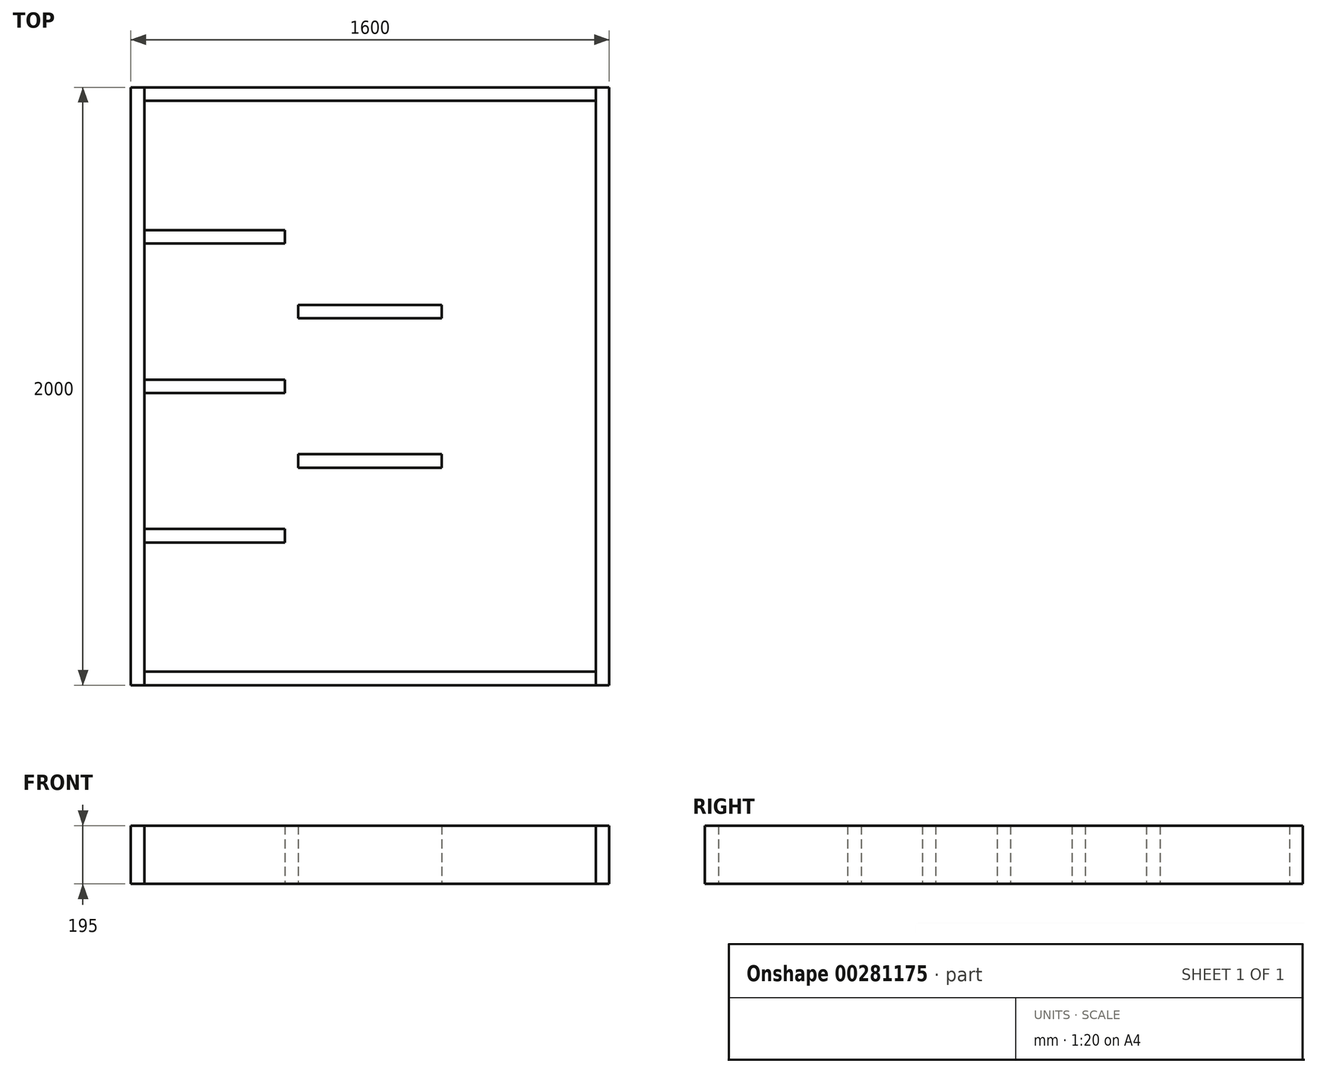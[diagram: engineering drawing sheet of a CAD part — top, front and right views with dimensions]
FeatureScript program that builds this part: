
annotation { "Feature Type Name" : "Feature", "Feature Type Description" : "" }
export const myFeature = defineFeature(function(context is Context, id is Id, definition is map)
    precondition{}
    {
        {
            var Q0;
            Q0=qCreatedBy(makeId("Top.planeOp"),FACE);
            var sketch = newSketch(context, id + "F0", { "sketchPlane" : qUnion([Q0])});
            skLineSegment(sketch, "E0.bottom", {"start": v(0, 0) * mm, "end": v(1700, 0) * mm, "construction": true});
            skLineSegment(sketch, "E0.top", {"start": v(0, 2500) * mm, "end": v(1700, 2500) * mm, "construction": true});
            skLineSegment(sketch, "E0.left", {"start": v(0, 0) * mm, "end": v(0, 2500) * mm, "construction": true});
            skLineSegment(sketch, "E0.right", {"start": v(1700, 0) * mm, "end": v(1700, 2500) * mm, "construction": true});
            skLineSegment(sketch, "E1.bottom", {"start": v(1700, 0) * mm, "end": v(1600, 0) * mm, "construction": true});
            skLineSegment(sketch, "E1.top", {"start": v(1700, 1050) * mm, "end": v(1600, 1050) * mm, "construction": true});
            skLineSegment(sketch, "E1.left", {"start": v(1700, 0) * mm, "end": v(1700, 1050) * mm, "construction": true});
            skLineSegment(sketch, "E1.right", {"start": v(1600, 0) * mm, "end": v(1600, 1050) * mm, "construction": true});
            skSolve(sketch);
        }
        {
            var Q0;
            Q0=qCreatedBy(makeId("Top.planeOp"),FACE);
            cPlane(context, id + "F1", {"entities" : qUnion([Q0]), "cplaneType" : CPlaneType.OFFSET, "offset" : 95 * mm, "width" : 150 * mm, "height" : 150 * mm});
        }
        {
            var Q0;
            Q0=qCreatedBy(id+"F1.planeOp",FACE);
            var sketch = newSketch(context, id + "F2", { "sketchPlane" : qUnion([Q0])});
            skLineSegment(sketch, "E2.bottom", {"start": v(0, 2305) * mm, "end": v(45, 2305) * mm});
            skLineSegment(sketch, "E2.top", {"start": v(0, 305) * mm, "end": v(45, 305) * mm});
            skLineSegment(sketch, "E2.left", {"start": v(0, 2305) * mm, "end": v(0, 305) * mm});
            skLineSegment(sketch, "E2.right", {"start": v(45, 2305) * mm, "end": v(45, 305) * mm});
            skLineSegment(sketch, "E3.bottom", {"start": v(1555, 2305) * mm, "end": v(1600, 2305) * mm});
            skLineSegment(sketch, "E3.top", {"start": v(1555, 305) * mm, "end": v(1600, 305) * mm});
            skLineSegment(sketch, "E3.left", {"start": v(1555, 2305) * mm, "end": v(1555, 305) * mm});
            skLineSegment(sketch, "E3.right", {"start": v(1600, 2305) * mm, "end": v(1600, 305) * mm});
            skLineSegment(sketch, "E4.bottom", {"start": v(45, 305) * mm, "end": v(1555, 305) * mm});
            skLineSegment(sketch, "E4.top", {"start": v(45, 350) * mm, "end": v(1555, 350) * mm});
            skLineSegment(sketch, "E4.left", {"start": v(45, 305) * mm, "end": v(45, 350) * mm});
            skLineSegment(sketch, "E4.right", {"start": v(1555, 305) * mm, "end": v(1555, 350) * mm});
            skLineSegment(sketch, "E5.bottom", {"start": v(45, 2305) * mm, "end": v(1555, 2305) * mm});
            skLineSegment(sketch, "E5.top", {"start": v(45, 2260) * mm, "end": v(1555, 2260) * mm});
            skLineSegment(sketch, "E5.left", {"start": v(45, 2305) * mm, "end": v(45, 2260) * mm});
            skLineSegment(sketch, "E5.right", {"start": v(1555, 2305) * mm, "end": v(1555, 2260) * mm});
            skLineSegment(sketch, "E6.bottom", {"start": v(515, 2260) * mm, "end": v(560, 2260) * mm});
            skLineSegment(sketch, "E6.top", {"start": v(515, 350) * mm, "end": v(560, 350) * mm});
            skLineSegment(sketch, "E6.left", {"start": v(515, 2260) * mm, "end": v(515, 350) * mm});
            skLineSegment(sketch, "E6.right", {"start": v(560, 2260) * mm, "end": v(560, 350) * mm});
            skLineSegment(sketch, "E7.bottom", {"start": v(1040, 2260) * mm, "end": v(1085, 2260) * mm});
            skLineSegment(sketch, "E7.top", {"start": v(1040, 350) * mm, "end": v(1085, 350) * mm});
            skLineSegment(sketch, "E7.left", {"start": v(1040, 2260) * mm, "end": v(1040, 350) * mm});
            skLineSegment(sketch, "E7.right", {"start": v(1085, 2260) * mm, "end": v(1085, 350) * mm});
            skLineSegment(sketch, "E8.bottom", {"start": v(45, 1827.5) * mm, "end": v(515, 1827.5) * mm});
            skLineSegment(sketch, "E8.top", {"start": v(45, 1782.5) * mm, "end": v(515, 1782.5) * mm});
            skLineSegment(sketch, "E8.left", {"start": v(45, 1827.5) * mm, "end": v(45, 1782.5) * mm});
            skLineSegment(sketch, "E8.right", {"start": v(515, 1827.5) * mm, "end": v(515, 1782.5) * mm});
            skLineSegment(sketch, "E9.bottom", {"start": v(45, 1327.5) * mm, "end": v(515, 1327.5) * mm});
            skLineSegment(sketch, "E9.top", {"start": v(45, 1282.5) * mm, "end": v(515, 1282.5) * mm});
            skLineSegment(sketch, "E9.left", {"start": v(45, 1327.5) * mm, "end": v(45, 1282.5) * mm});
            skLineSegment(sketch, "E9.right", {"start": v(515, 1327.5) * mm, "end": v(515, 1282.5) * mm});
            skLineSegment(sketch, "E10.bottom", {"start": v(45, 827.5) * mm, "end": v(515, 827.5) * mm});
            skLineSegment(sketch, "E10.top", {"start": v(45, 782.5) * mm, "end": v(515, 782.5) * mm});
            skLineSegment(sketch, "E10.left", {"start": v(45, 827.5) * mm, "end": v(45, 782.5) * mm});
            skLineSegment(sketch, "E10.right", {"start": v(515, 827.5) * mm, "end": v(515, 782.5) * mm});
            skPoint(sketch, "E11", {"position": v(45, 1305) * mm});
            skPoint(sketch, "E12", {"position": v(45, 805) * mm});
            skPoint(sketch, "E13", {"position": v(45, 1805) * mm});
            skLineSegment(sketch, "E14.bottom", {"start": v(560, 1577.5) * mm, "end": v(1040, 1577.5) * mm});
            skLineSegment(sketch, "E14.top", {"start": v(560, 1532.5) * mm, "end": v(1040, 1532.5) * mm});
            skLineSegment(sketch, "E14.left", {"start": v(560, 1577.5) * mm, "end": v(560, 1532.5) * mm});
            skLineSegment(sketch, "E14.right", {"start": v(1040, 1577.5) * mm, "end": v(1040, 1532.5) * mm});
            skLineSegment(sketch, "E15.bottom", {"start": v(560, 1077.5) * mm, "end": v(1040, 1077.5) * mm});
            skLineSegment(sketch, "E15.top", {"start": v(560, 1032.5) * mm, "end": v(1040, 1032.5) * mm});
            skLineSegment(sketch, "E15.left", {"start": v(560, 1077.5) * mm, "end": v(560, 1032.5) * mm});
            skLineSegment(sketch, "E15.right", {"start": v(1040, 1077.5) * mm, "end": v(1040, 1032.5) * mm});
            skPoint(sketch, "E16", {"position": v(560, 1555) * mm});
            skPoint(sketch, "E17", {"position": v(560, 1055) * mm});
            skLineSegment(sketch, "E18", {"start": v(800, 2260) * mm, "end": v(800, 350) * mm, "construction": true});
            skLineSegment(sketch, "E19.MirrorCS", {"start": v(1085, 827.5) * mm, "end": v(1085, 782.5) * mm});
            skLineSegment(sketch, "E20.MirrorCS", {"start": v(1555, 1827.5) * mm, "end": v(1555, 1782.5) * mm});
            skLineSegment(sketch, "E21.MirrorCS", {"start": v(1085, 1827.5) * mm, "end": v(1085, 1782.5) * mm});
            skLineSegment(sketch, "E22.MirrorCS", {"start": v(1555, 827.5) * mm, "end": v(1555, 782.5) * mm});
            skLineSegment(sketch, "E23.MirrorCS", {"start": v(1085, 1327.5) * mm, "end": v(1085, 1282.5) * mm});
            skLineSegment(sketch, "E24.MirrorCS", {"start": v(1555, 1327.5) * mm, "end": v(1555, 1282.5) * mm});
            skPoint(sketch, "E25.MirrorP", {"position": v(1555, 1305) * mm});
            skPoint(sketch, "E26.MirrorP", {"position": v(1040, 1555) * mm});
            skLineSegment(sketch, "E27.MirrorCS", {"start": v(1555, 1282.5) * mm, "end": v(1085, 1282.5) * mm});
            skPoint(sketch, "E28.MirrorP", {"position": v(1555, 805) * mm});
            skLineSegment(sketch, "E29.MirrorCS", {"start": v(1555, 1782.5) * mm, "end": v(1085, 1782.5) * mm});
            skLineSegment(sketch, "E30.MirrorCS", {"start": v(1555, 1327.5) * mm, "end": v(1085, 1327.5) * mm});
            skLineSegment(sketch, "E31.MirrorCS", {"start": v(1555, 827.5) * mm, "end": v(1085, 827.5) * mm});
            skLineSegment(sketch, "E32.MirrorCS", {"start": v(1555, 1827.5) * mm, "end": v(1085, 1827.5) * mm});
            skPoint(sketch, "E33.MirrorP", {"position": v(1040, 1055) * mm});
            skLineSegment(sketch, "E34.MirrorCS", {"start": v(1555, 782.5) * mm, "end": v(1085, 782.5) * mm});
            skPoint(sketch, "E35.MirrorP", {"position": v(1555, 1805) * mm});
            skSolve(sketch);
        }
        {
            var Q0;
            Q0=makeQuery(id+"F2.imprint","IMPRINT",FACE,{"disambiguationData":[TD([[makeQuery(id+"F2.imprint","IMPRINT",EDGE,{"derivedFrom":sQuery(id+"F2.wireOp",EDGE,"E2.bottom")}),-1.0]])]});
            var Q1;
            {var subQ6=sQuery(id+"F2.wireOp",EDGE,"E6.bottom");Q1=makeQuery(id+"F2.imprint","IMPRINT",FACE,{"disambiguationData":[TD([[makeQuery(id+"F2.imprint","IMPRINT",EDGE,{"derivedFrom":subQ6}),-1.0]])]});}
            var Q2;
            {var subQ6=sQuery(id+"F2.wireOp",EDGE,"E7.bottom");Q2=makeQuery(id+"F2.imprint","IMPRINT",FACE,{"disambiguationData":[TD([[makeQuery(id+"F2.imprint","IMPRINT",EDGE,{"derivedFrom":subQ6}),-1.0]])]});}
            var Q3;
            Q3=makeQuery(id+"F2.imprint","IMPRINT",FACE,{"disambiguationData":[TD([[makeQuery(id+"F2.imprint","IMPRINT",EDGE,{"derivedFrom":sQuery(id+"F2.wireOp",EDGE,"E3.bottom")}),-1.0]])]});
            extrude(context, id + "F3", {"entities" : qUnion([Q0, Q1, Q2, Q3]), "depth" : 195 * mm});
        }
        {
            var Q0;
            Q0=makeQuery(id+"F2.imprint","IMPRINT",FACE,{"disambiguationData":[TD([[makeQuery(id+"F2.imprint","IMPRINT",EDGE,{"derivedFrom":sQuery(id+"F2.wireOp",EDGE,"E5.bottom")}),-1.0]])]});
            var Q1;
            Q1=makeQuery(id+"F2.imprint","IMPRINT",FACE,{"disambiguationData":[TD([[makeQuery(id+"F2.imprint","IMPRINT",EDGE,{"derivedFrom":sQuery(id+"F2.wireOp",EDGE,"E8.bottom")}),-1.0]])]});
            var Q2;
            Q2=makeQuery(id+"F2.imprint","IMPRINT",FACE,{"disambiguationData":[TD([[makeQuery(id+"F2.imprint","IMPRINT",EDGE,{"derivedFrom":sQuery(id+"F2.wireOp",EDGE,"E9.bottom")}),-1.0]])]});
            var Q3;
            Q3=makeQuery(id+"F2.imprint","IMPRINT",FACE,{"disambiguationData":[TD([[makeQuery(id+"F2.imprint","IMPRINT",EDGE,{"derivedFrom":sQuery(id+"F2.wireOp",EDGE,"E10.bottom")}),-1.0]])]});
            var Q4;
            Q4=makeQuery(id+"F2.imprint","IMPRINT",FACE,{"disambiguationData":[TD([[makeQuery(id+"F2.imprint","IMPRINT",EDGE,{"derivedFrom":sQuery(id+"F2.wireOp",EDGE,"E4.bottom")}),1.0]])]});
            var Q5;
            Q5=makeQuery(id+"F2.imprint","IMPRINT",FACE,{"disambiguationData":[TD([[makeQuery(id+"F2.imprint","IMPRINT",EDGE,{"derivedFrom":sQuery(id+"F2.wireOp",EDGE,"E15.bottom")}),-1.0]])]});
            var Q6;
            Q6=makeQuery(id+"F2.imprint","IMPRINT",FACE,{"disambiguationData":[TD([[makeQuery(id+"F2.imprint","IMPRINT",EDGE,{"derivedFrom":sQuery(id+"F2.wireOp",EDGE,"E14.bottom")}),-1.0]])]});
            var Q7;
            Q7=makeQuery(id+"F2.imprint","IMPRINT",FACE,{"disambiguationData":[TD([[makeQuery(id+"F2.imprint","IMPRINT",EDGE,{"derivedFrom":sQuery(id+"F2.wireOp",EDGE,"E20.MirrorCS")}),-1.0]])]});
            var Q8;
            Q8=makeQuery(id+"F2.imprint","IMPRINT",FACE,{"disambiguationData":[TD([[makeQuery(id+"F2.imprint","IMPRINT",EDGE,{"derivedFrom":sQuery(id+"F2.wireOp",EDGE,"E23.MirrorCS")}),1.0]])]});
            var Q9;
            Q9=makeQuery(id+"F2.imprint","IMPRINT",FACE,{"disambiguationData":[TD([[makeQuery(id+"F2.imprint","IMPRINT",EDGE,{"derivedFrom":sQuery(id+"F2.wireOp",EDGE,"E19.MirrorCS")}),1.0]])]});
            extrude(context, id + "F4", {"entities" : qUnion([Q0, Q1, Q2, Q3, Q4, Q5, Q6, Q7, Q8, Q9]), "depth" : 195 * mm});
        }
    });
